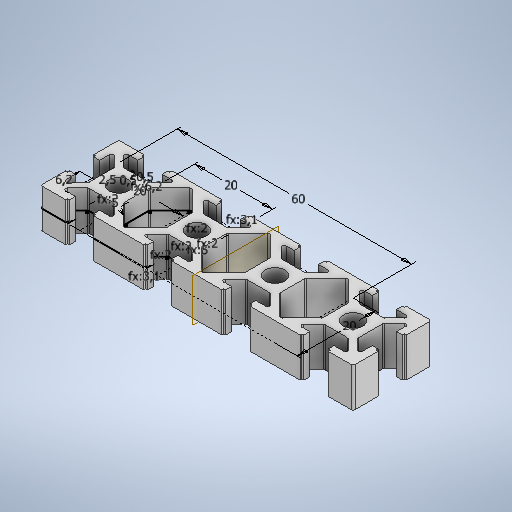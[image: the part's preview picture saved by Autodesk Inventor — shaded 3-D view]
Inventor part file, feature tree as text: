
AUTODESK INVENTOR PART (.ipt)
format: ipt  version: 2025.2 (Build 292293000, 293)  size: 582,656 bytes
history: native  units: mm
features: other x2, extrude x2, sketch x1, pattern_linear x1, mirror x1
ambient origin geometry x8: Origin, YZ Plane, XZ Plane, XY Plane, X Axis, Y Axis, Z Axis, Center Point
bodies: Body1 (feature_tree)
feature tree (7):
  other  "Sólido1"
  sketch  "Esboço1"  dims[d0=20.0mm d2=5.0mm d4=2.0mm d7=0.5mm d8=2.0mm d17=5.0mm d18=6.2mm d23=2.0mm d25=0.5mm d26=2.5mm d27=6.2mm d29=20.0mm d30=5.0mm d31=60.0mm d32=20.0mm d33=2.0mm d34=3.1mm d35=2.0mm d36=2.0mm d37=3.1mm d38=2.0mm d39=10.0mm d40=0.0mm d41=30.0mm d43=20.0mm d44=10.0mm d45=0.0mm d19=0.5mm d20=0.872665mm d42=0.872665mm]
  extrude  "Extrusão1"  Depth=5.0mm
  pattern_linear  "Padrão retangular1"  Spacing1=2.0mm  [1 undecoded]
  other  "Plano de trabalho1"
  extrude  "Extrusão2"  Depth=0.5mm
  mirror  "Espelhar3"
note: 1 required parameter value undecoded (feature->parameter linkage not recoverable at this tier; creation-order binding heuristic only, values carry confidence <= 0.55)
